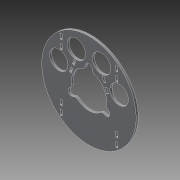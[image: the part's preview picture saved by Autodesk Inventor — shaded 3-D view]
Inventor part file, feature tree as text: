
AUTODESK INVENTOR PART (.ipt)
format: ipt  version: 2022 (Build 260153000, 153)  size: 207,360 bytes
history: native  units: mm
features: other x6, extrude x2, sketch x2, fillet x1, pattern_circular x1, reference x1
ambient origin geometry x8: Origin, YZ Plane, XZ Plane, XY Plane, X Axis, Y Axis, Z Axis, Center Point
bodies: Body1 (feature_tree)
feature tree (13):
  other  "Твердое тело1"
  other  "РабПлоскость1"
  extrude  "Выдавливание1"  Depth=6.0mm TaperAngle=0.0deg
  extrude  "Выдавливание2"  Depth=53.0mm
  fillet  "Сопряжение1"  Radius=20.0mm
  pattern_circular  "Круговой массив1"  [2 undecoded]
  sketch  "Эскиз1"
  reference  "Ссылка1"
  sketch  "Эскиз2"
  parser-record x1  (decoder bookkeeping rows leaked as tree rows — omitted from the tree; the rows remain in map.json)
  other  "Поворотный_модуль_В5.iam"
  other  "Основание емкости:1"
  other  "Стойка_В5:5"
note: 2 required parameter values undecoded (feature->parameter linkage not recoverable at this tier; creation-order binding heuristic only, values carry confidence <= 0.55)
note: 1 file-system path scrubbed to <path> (originals preserved in map.json)
